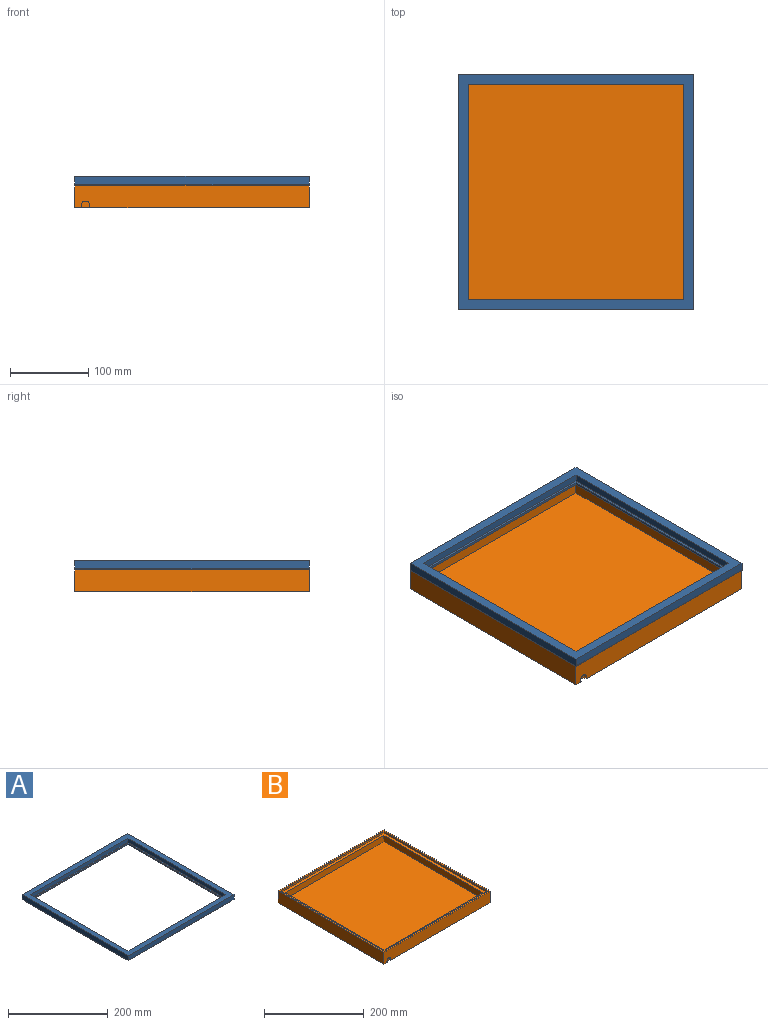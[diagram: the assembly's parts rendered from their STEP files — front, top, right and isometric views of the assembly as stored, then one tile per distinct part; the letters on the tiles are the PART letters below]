
ASSEMBLY  parts=2 mates=1
PART A: 25 faces, bbox 300.1x300.1x15.4 mm
  f0: plane 300.1x11.37mm, normal (-1,0,0), area 3410.9mm2, adj f5,f10,f15,f17
  f1: plane 275.7x9.37mm, normal (1,0,0), area 2582.2mm2, adj f6,f11,f17,f19
  f2: plane 282.2x3mm, normal (1,0,0), area 846.6mm2, adj f7,f12,f19,f21
  f3: plane 276.2x3mm, normal (1,0,0), area 828.6mm2, adj f8,f13,f21,f23
  f4: plane 292.1x4mm, normal (-1,0,0), area 1168.4mm2, adj f9,f14,f15,f23
  f5: plane 300.1x11.37mm, normal (0,-1,0), area 3410.9mm2, adj f0,f15,f16,f17
  f6: plane 275.7x9.37mm, normal (0,1,0), area 2582.2mm2, adj f1,f17,f18,f19
  f7: plane 282.2x3mm, normal (0,1,0), area 846.6mm2, adj f2,f19,f20,f21
  f8: plane 276.2x3mm, normal (0,1,0), area 828.6mm2, adj f3,f21,f22,f23
  f9: plane 292.1x4mm, normal (0,-1,0), area 1168.4mm2, adj f4,f15,f23,f24
  f10: plane 300.1x11.37mm, normal (0,1,0), area 3410.9mm2, adj f0,f15,f16,f17
  f11: plane 275.7x9.37mm, normal (0,-1,0), area 2582.2mm2, adj f1,f17,f18,f19
  f12: plane 282.2x3mm, normal (0,-1,0), area 846.6mm2, adj f2,f19,f20,f21
  f13: plane 276.2x3mm, normal (0,-1,0), area 828.6mm2, adj f3,f21,f22,f23
  f14: plane 292.1x4mm, normal (0,1,0), area 1168.4mm2, adj f4,f15,f23,f24
  f15: plane 300.1x300.1mm, normal (0,0,-1), area 4737.6mm2, adj f0,f4,f5,f9,f10,f14,f16,f24
  f16: plane 300.1x11.37mm, normal (1,0,0), area 3410.9mm2, adj f5,f10,f15,f17
  f17: plane 300.1x300.1mm, normal (0,0,1), area 14049.5mm2, adj f0,f1,f5,f6,f10,f11,f16,f18
  f18: plane 275.7x9.37mm, normal (-1,0,0), area 2582.2mm2, adj f6,f11,f17,f19
  f19: plane 282.2x282.2mm, normal (0,0,-1), area 3626.3mm2, adj f1,f2,f6,f7,f11,f12,f18,f20
  f20: plane 282.2x3mm, normal (-1,0,0), area 846.6mm2, adj f7,f12,f19,f21
  f21: plane 282.2x282.2mm, normal (0,0,1), area 3350.4mm2, adj f2,f3,f7,f8,f12,f13,f20,f22
  f22: plane 276.2x3mm, normal (-1,0,0), area 828.6mm2, adj f8,f13,f21,f23
  f23: plane 292.1x292.1mm, normal (0,0,-1), area 9036mm2, adj f3,f4,f8,f9,f13,f14,f22,f24
  f24: plane 292.1x4mm, normal (1,0,0), area 1168.4mm2, adj f9,f14,f15,f23
PART B: 18 faces, bbox 300x300x29 mm
  f0: plane 300x29mm, normal (0,-1,0), area 8623.6mm2, adj f2,f3,f4,f5,f11
  f1: plane 300x29mm, normal (0,1,0), area 8700mm2, adj f2,f3,f4,f11
  f2: plane 300x29mm, normal (-1,0,0), area 8700mm2, adj f0,f1,f4,f11
  f3: plane 300x29mm, normal (1,0,0), area 8700mm2, adj f0,f1,f4,f11
  f4: plane 300x300mm, normal (0,0,-1), area 89964.1mm2, adj f0,f1,f2,f3,f5,f6
  f5: cylinder r=5.4mm len=10.79mm, axis (0,-1,0), area 93.3mm2, adj f0,f4,f6
  f6: plane 10.79x8.4mm, normal (0,-1,0), area 76.4mm2, adj f4,f5
  f7: plane 292x4mm, normal (0,-1,0), area 1168mm2, adj f8,f10,f11,f17
  f8: plane 292x4mm, normal (-1,0,0), area 1168mm2, adj f7,f9,f11,f17
  f9: plane 292x4mm, normal (0,1,0), area 1168mm2, adj f8,f10,f11,f17
  f10: plane 292x4mm, normal (1,0,0), area 1168mm2, adj f7,f9,f11,f17
  f11: plane 300x300mm, normal (0,0,1), area 4736mm2, adj f0,f1,f2,f3,f7,f8,f9,f10
  f12: plane 280x280mm, normal (0,0,1), area 78400mm2, adj f13,f14,f15,f16
  f13: plane 280x15mm, normal (0,1,0), area 4200mm2, adj f12,f14,f16,f17
  f14: plane 280x15mm, normal (-1,0,0), area 4200mm2, adj f12,f13,f15,f17
  f15: plane 280x15mm, normal (0,-1,0), area 4200mm2, adj f12,f14,f16,f17
  f16: plane 280x15mm, normal (1,0,0), area 4200mm2, adj f12,f13,f15,f17
  f17: plane 292x292mm, normal (0,0,1), area 6864mm2, adj f7,f8,f9,f10,f13,f14,f15,f16
PLACE A t=(-75.19,16.66,68.47)mm
PLACE B t=(-164.55,-79.49,43.52)mm
MATE parallel B.f17 <-> A.f23  axis (0,0,1) through (-209.02,9.86,68.52)mm
